# Revit family: 307_1eced028aad84f27b3608c036c9cce
name_source: partatom
category: Pipe Accessories
units: mm (PartAtom-declared; Revit-internal decimal feet)

## family parameters
Always vertical = Yes
Cut with Voids When Loaded = No
Part Type = Breaks Into
Round Connector Dimension = Use Diameter
Shared = No
Work Plane-Based = No

## types (5) — shared parameters
CenSd_R6_6 = 9 mm
Description = Deaerator, swiveling air vent, F-F conn., max. press. 10 bar
L12 = 10 mm  [stored 0.0328084 ft]
L16 = 8 mm  [stored 0.0262467 ft]
L22 = 2 mm  [stored 0.00656168 ft]
L22__ve = -2 mm  [stored -0.00656168 ft]
L2D = 109 mm
L2D_Min = 3048 mm
L3 = 3 mm  [stored 0.00984252 ft]
L4 = 4 mm  [stored 0.0131234 ft]
L5 = 5 mm  [stored 0.0164042 ft]
L6 = 6 mm  [stored 0.019685 ft]
LLL = 20 mm  [stored 0.0656168 ft]
Manufacturer = FAR
QmdConnectorList = 301;D;302;D
R6 = 10 mm  [stored 0.0328084 ft]
R8 = 11 mm  [stored 0.0360892 ft]
R9 = 12 mm  [stored 0.0393701 ft]
R9__ve = -12 mm  [stored -0.0393701 ft]
W2D = 25 mm  [stored 0.082021 ft]
WWW = 40 mm
magiPartTypeId = 307
magiProductFamilyId = 1eced028aad84f27b3608c036c9cce
zero-valued in all types: Default Elevation

## per-type parameters (varying)
| type | A | B | B4 | CenSd_R3_6 | D | HH | L2 | LL | LNT | LNT__ve | NT | NT__ve | R | R1 | R15 | R2 | R22 | R222C | R222S | R23 | R3 | R4 | R7 | magiProductId |
| 2250 1 | 51 mm | 134 mm | 34 mm | 16 mm  [stored 0.0524934 ft] | 25 mm | 59 mm | 55 mm | 28 mm  [stored 0.0918635 ft] | 94 mm | -94 mm | 7 mm | -7 mm | 13 mm  [stored 0.0426509 ft] | 44 mm | 22 mm  [stored 0.0721785 ft] | 40 mm | 30 mm  [stored 0.0984252 ft] | 29 mm | 12 mm  [stored 0.0393701 ft] | 31 mm  [stored 0.101706 ft] | 19 mm | 15 mm  [stored 0.0492126 ft] | 43 mm | 98dc00267bbd458999a4ee0bc8f6cd |
| 2250 112 | 56 mm | 149 mm | 37 mm | 23 mm | 40 mm | 70 mm | 60 mm | 33 mm  [stored 0.108268 ft] | 103 mm | -103 mm | 8 mm  [stored 0.0262467 ft] | -8 mm  [stored -0.0262467 ft] | 20 mm  [stored 0.0656168 ft] | 48 mm | 26 mm  [stored 0.0853018 ft] | 44 mm | 34 mm | 33 mm  [stored 0.108268 ft] | 14 mm  [stored 0.0459318 ft] | 35 mm | 26 mm  [stored 0.0853018 ft] | 22 mm  [stored 0.0721785 ft] | 47 mm | 601f24ca172b43ae870b4dcd4e0103 |
| 2250 114 | 56 mm | 149 mm | 37 mm | 19 mm | 32 mm | 70 mm | 60 mm | 33 mm  [stored 0.108268 ft] | 103 mm | -103 mm | 8 mm  [stored 0.0262467 ft] | -8 mm  [stored -0.0262467 ft] | 16 mm  [stored 0.0524934 ft] | 48 mm | 26 mm  [stored 0.0853018 ft] | 44 mm | 34 mm | 33 mm  [stored 0.108268 ft] | 14 mm  [stored 0.0459318 ft] | 35 mm | 22 mm  [stored 0.0721785 ft] | 18 mm  [stored 0.0590551 ft] | 47 mm | 970a3e65d21e4edd951672e02dc173 |
| 2250 2 | 61 mm | 145 mm | 36 mm | 27 mm  [stored 0.0885827 ft] | 50 mm | 67 mm | 63 mm | 38 mm | 109 mm | -109 mm | 8 mm  [stored 0.0262467 ft] | -8 mm  [stored -0.0262467 ft] | 25 mm  [stored 0.082021 ft] | 50 mm | 28 mm  [stored 0.0918635 ft] | 46 mm | 36 mm | 35 mm | 15 mm  [stored 0.0492126 ft] | 37 mm | 31 mm  [stored 0.101706 ft] | 27 mm  [stored 0.0885827 ft] | 50 mm | f20e4d894263487d818821c8701416 |
| 2250 34 | 51 mm | 134 mm | 34 mm | 14 mm  [stored 0.0459318 ft] | 20 mm | 59 mm | 55 mm | 28 mm  [stored 0.0918635 ft] | 94 mm | -94 mm | 7 mm | -7 mm | 10 mm  [stored 0.0328084 ft] | 44 mm | 22 mm  [stored 0.0721785 ft] | 40 mm | 30 mm  [stored 0.0984252 ft] | 29 mm | 12 mm  [stored 0.0393701 ft] | 31 mm  [stored 0.101706 ft] | 16 mm  [stored 0.0524934 ft] | 12 mm  [stored 0.0393701 ft] | 43 mm | 4f131df2afce4f1fbfe8ea47d54976 |

note: column(s) folded — value = type name in every type: MC Product Code

note: [stored X ft] marks values corroborated as IEEE doubles in the binary element streams (Revit-internal decimal feet)

## geometry (parser evidence)
native form markers: Sweep x2
no freeform markers — native parametric forms only
